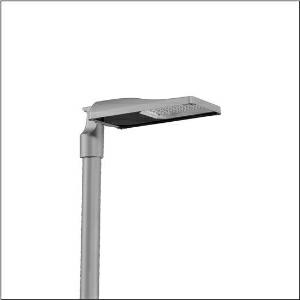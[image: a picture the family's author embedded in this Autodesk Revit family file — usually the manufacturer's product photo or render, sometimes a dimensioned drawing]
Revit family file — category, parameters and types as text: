
# Revit family: streetlight_sl_31_mini___st1_0a_5xh6d3aa08ga_9e06
name_source: partatom
category: Lighting Fixtures
units: mm (PartAtom-declared; Revit-internal decimal feet)

## family parameters
Cut with Voids When Loaded = No
Host = Face
Light Source = No
Part Type = Normal
Room Calculation Point = No
Round Connector Dimension = Use Diameter
Shared = No

## types (1)
- --- (1 x LED, 5710 lm, 37.3 W, 3000K)
    Apparent Load = 37 VA
    CIE Flux Codes = 37 72 97 100 100
    Color Rendering = 70
    Color Temperature = 3000K
    Default Elevation = 1800 mm
    Description = Streetlight SL 31 mini Easy mast luminaire for post-top, side-entry; light control with lens of PMMA; light distribution: ST1.0a, direct asymmetric distribution, for standard-compliant lighting for roads and squares; LED: luminous flux: 5.710lm, light colour: 730, colour temperature: 3000K; luminous efficacy: 153,1lm/W; control: pre-setting: linear dimming characteristic, flexible luminous flux parameterisation, time-dependent luminous flux control, constant luminous flux control, intelligent temperature release in ECG and LED module, overheat protection; luminaire housing, of diecast aluminium, Siteco® metallic grey (DB 702S), corrosivity category C5 high according to DIN EN ISO 12944; cover of toughened safety glass, transparent, opened without tools; mast flange of diecast aluminium, Siteco® metallic grey (DB 702S), spigot size: 76/60mm, mast flange included unmounted; with cable H07RN-F 2x 1.5mm², cable length: 6,5m, connection cable pre-assembled; mains connection: 220..240V, AC, 50/60Hz; power consumption (at start of service life): 37,3W / (at end of service life): 38,7W / (with reduced operation 50%): 17,5W; protection rating (complete): IP66; insulation class (complete): insulation class II (safety insulation); impact resistance: IK10; certification: CE, ENEC, ENEC+, VDE, UKCA; permissible operating ambient temperature for outdoor applications: -40..+50°C; packaging unit: 1 piece

Light Distribution: ST1.0a
    Height = 76 mm
    Lamp = 1 x LED
    Lamp Light Flux = 5710 lm
    Lamp Power = 37.3 W
    Lamp count = 1
    Length = 547 mm
    Luminous efficacy = 153 lm/W
    Manufacturer = Siteco
    ModVariant = No
    Model = 5XH6D3AA08GA
    Number of Poles = 1
    OnlyDefault = Yes
    Power Factor = 1
    Product Name = Streetlight SL 31 mini | ST1.0a
    Product group = mast luminaire | pylon top
    ProductGroupID = 6100
    Protection Class = Protection class II
    Protection Degree = IP 66
    RLX_Detail_Level = 1
    RLX_Emergency_Light_Flux = 0 lm
    RLX_Emergency_Type = 0
    RLX_Emergency_Type_DB = No
    RlxData = <blob elided: 39461 chars, md5=d810582f>
    Socket = socket
    Standby Power = 0 W
    System Light Flux = 5710 lm
    System Power = 37 W
    Type Comments = factory setting: luminous flux: 100 % | dim-lin: 254 | 386 mA
    Type Image = l_1300326.jpg
    URL = http://relux.com
    VarID = @adj_054348
    Voltage = 0 V
    Weight = 0.00 kg
    Width = 265 mm

## geometry (parser evidence)
native form markers: Blend x4, Sweep x11
no freeform markers — native parametric forms only
